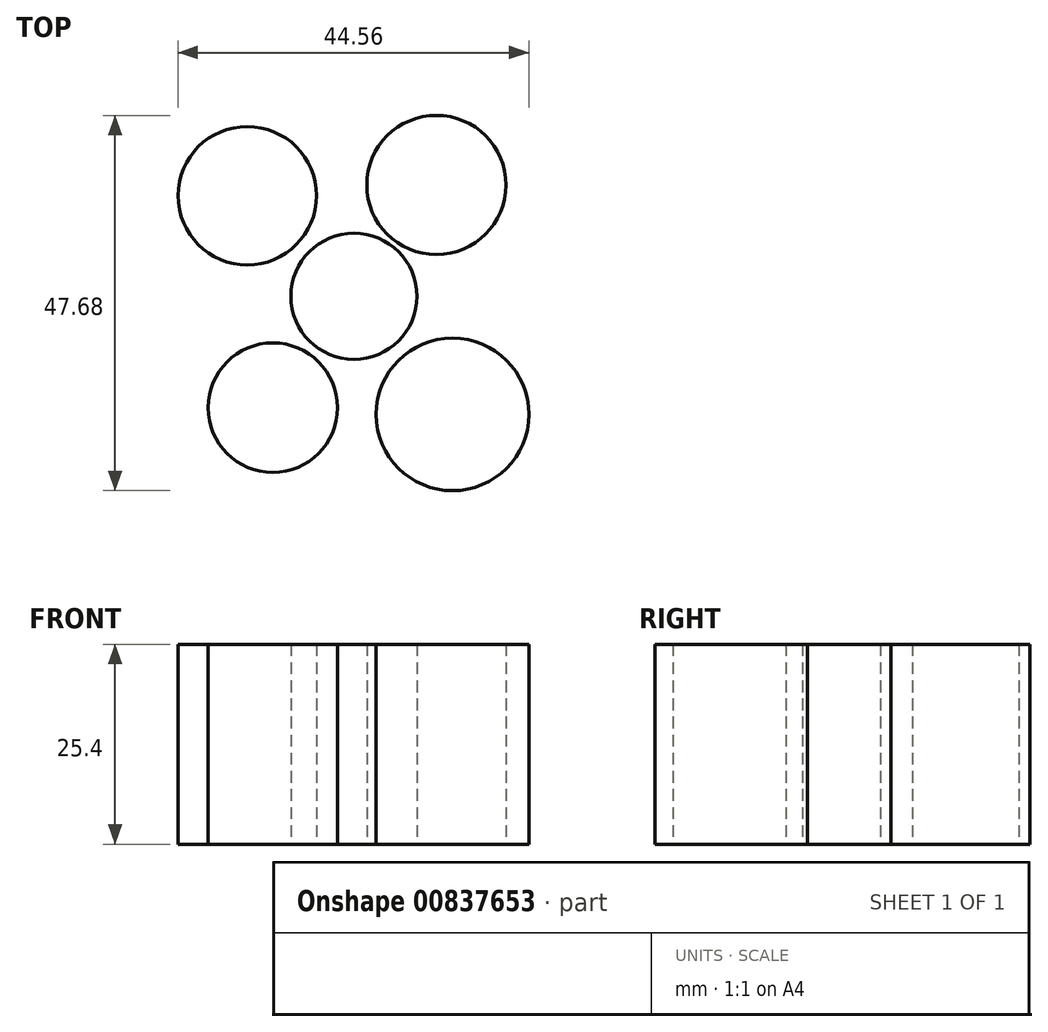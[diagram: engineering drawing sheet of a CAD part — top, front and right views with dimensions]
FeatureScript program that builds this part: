
annotation { "Feature Type Name" : "Feature", "Feature Type Description" : "" }
export const myFeature = defineFeature(function(context is Context, id is Id, definition is map)
    precondition{}
    {
        {
            var Q0;
            Q0=qCreatedBy(makeId("Top.planeOp"),FACE);
            var sketch = newSketch(context, id + "F0", { "sketchPlane" : qUnion([Q0])});
            skCircle(sketch, "E0", {"center": v(0, 0) * mm, "radius": 8 * mm});
            skCircle(sketch, "E1", {"center": v(10.48, 14.14) * mm, "radius": 8.84 * mm});
            skCircle(sketch, "E2", {"center": v(-13.55, 12.78) * mm, "radius": 8.8 * mm});
            skCircle(sketch, "E3", {"center": v(-10.3, -14.14) * mm, "radius": 8.23 * mm});
            skCircle(sketch, "E4", {"center": v(12.53, -15) * mm, "radius": 9.7 * mm});
            skLineSegment(sketch, "E5", {"start": v(13.78, 5.94) * mm, "end": v(9.7, 0) * mm});
            skLineSegment(sketch, "E6", {"start": v(9.7, 0) * mm, "end": v(13.53, -5.36) * mm});
            skLineSegment(sketch, "E7", {"start": v(-2.8, -17.5) * mm, "end": v(0, -14.32) * mm});
            skLineSegment(sketch, "E8", {"start": v(0, -14.32) * mm, "end": v(3.04, -17) * mm});
            skLineSegment(sketch, "E9", {"start": v(-13.37, 3.98) * mm, "end": v(-10.45, 0) * mm});
            skLineSegment(sketch, "E10", {"start": v(-10.45, 0) * mm, "end": v(-13.05, -6.39) * mm});
            skLineSegment(sketch, "E11", {"start": v(-5.19, 10.04) * mm, "end": v(-1.71, 8.94) * mm});
            skLineSegment(sketch, "E12", {"start": v(-1.71, 8.94) * mm, "end": v(2.23, 10.96) * mm});
            skSolve(sketch);
        }
        {
            var Q0;
            Q0=qCreatedBy(makeId("Top.planeOp"),FACE);
            var sketch = newSketch(context, id + "F1", { "sketchPlane" : qUnion([Q0])});
            skSolve(sketch);
        }
        {
            var Q0;
            Q0 = qSketchRegion(id + "F1", true);
            var Q1;
            {var subQ0=sQuery(id+"F0.wireOp",EDGE,"E2");var subQ1=makeQuery(id+"F0.imprint","INTERSECT",VERTEX,{"derivedFrom":[subQ0,sQuery(id+"F0.wireOp",EDGE,"E9")]});Q1=makeQuery(id+"F0.imprint","IMPRINT",FACE,{"disambiguationData":[TD([[makeQuery(id+"F0.imprint","IMPRINT",EDGE,{"disambiguationData":[TD([[subQ1,-1.0]])],"derivedFrom":subQ0}),1.0]])]});}
            var Q2;
            {var subQ0=sQuery(id+"F0.wireOp",EDGE,"E1");var subQ1=makeQuery(id+"F0.imprint","INTERSECT",VERTEX,{"derivedFrom":[subQ0,sQuery(id+"F0.wireOp",EDGE,"E5")]});Q2=makeQuery(id+"F0.imprint","IMPRINT",FACE,{"disambiguationData":[TD([[makeQuery(id+"F0.imprint","IMPRINT",EDGE,{"disambiguationData":[TD([[subQ1,1.0]])],"derivedFrom":subQ0}),1.0]])]});}
            var Q3;
            {var subQ0=sQuery(id+"F0.wireOp",EDGE,"E4");var subQ1=makeQuery(id+"F0.imprint","INTERSECT",VERTEX,{"derivedFrom":[subQ0,sQuery(id+"F0.wireOp",EDGE,"E6")]});Q3=makeQuery(id+"F0.imprint","IMPRINT",FACE,{"disambiguationData":[TD([[makeQuery(id+"F0.imprint","IMPRINT",EDGE,{"disambiguationData":[TD([[subQ1,-1.0]])],"derivedFrom":subQ0}),1.0]])]});}
            var Q4;
            {var subQ0=sQuery(id+"F0.wireOp",EDGE,"E3");var subQ1=makeQuery(id+"F0.imprint","INTERSECT",VERTEX,{"derivedFrom":[subQ0,sQuery(id+"F0.wireOp",EDGE,"E7")]});Q4=makeQuery(id+"F0.imprint","IMPRINT",FACE,{"disambiguationData":[TD([[makeQuery(id+"F0.imprint","IMPRINT",EDGE,{"disambiguationData":[TD([[subQ1,1.0]])],"derivedFrom":subQ0}),1.0]])]});}
            var Q5;
            Q5=makeQuery(id+"F0.imprint","IMPRINT",FACE,{"disambiguationData":[TD([[makeQuery(id+"F0.imprint","IMPRINT",EDGE,{"derivedFrom":sQuery(id+"F0.wireOp",EDGE,"E0")}),1.0]])]});
            extrude(context, id + "F2", {"entities" : qUnion([Q0, Q1, Q2, Q3, Q4, Q5]), "depth" : 25.4 * mm, "offsetDistance" : 25.4 * mm});
        }
    });
